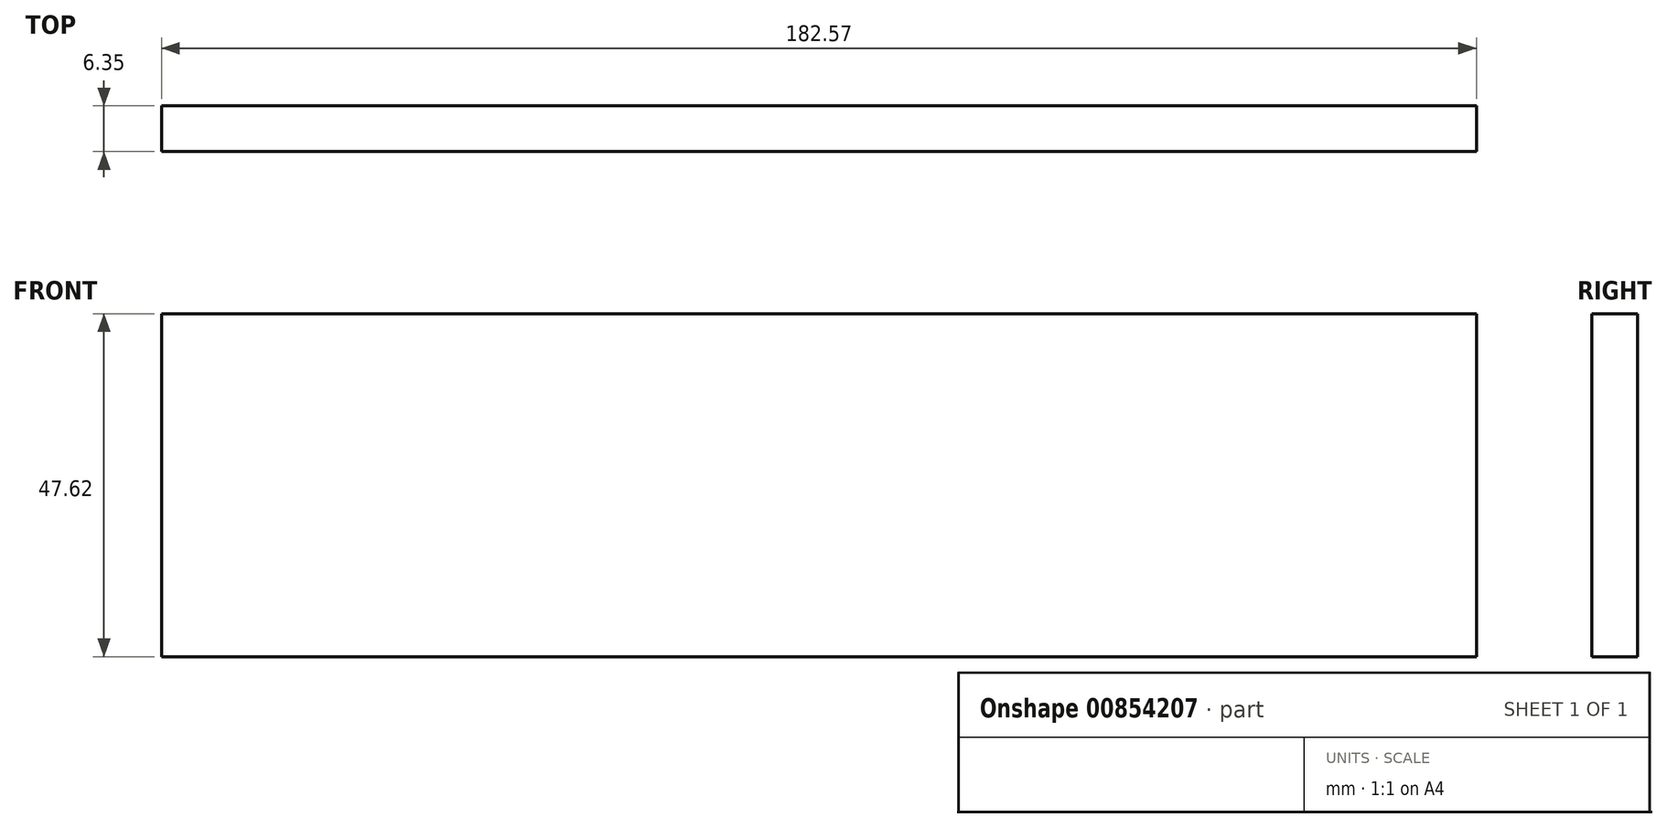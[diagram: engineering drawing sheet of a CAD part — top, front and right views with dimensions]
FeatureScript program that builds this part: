
annotation { "Feature Type Name" : "Feature", "Feature Type Description" : "" }
export const myFeature = defineFeature(function(context is Context, id is Id, definition is map)
    precondition{}
    {
        {
            var Q0;
            Q0=qCreatedBy(makeId("Front.planeOp"),FACE);
            var sketch = newSketch(context, id + "F0", { "sketchPlane" : qUnion([Q0])});
            skLineSegment(sketch, "E0.bottom", {"start": v(-91.29, 23.81) * mm, "end": v(91.28, 23.81) * mm});
            skLineSegment(sketch, "E0.top", {"start": v(-91.29, -23.81) * mm, "end": v(91.28, -23.81) * mm});
            skLineSegment(sketch, "E0.left", {"start": v(-91.29, 23.81) * mm, "end": v(-91.29, -23.81) * mm});
            skLineSegment(sketch, "E0.right", {"start": v(91.28, 23.81) * mm, "end": v(91.28, -23.81) * mm});
            skSolve(sketch);
        }
        {
            var Q0;
            Q0=makeQuery(id+"F0.imprint","IMPRINT",FACE,{"disambiguationData":[TD([[makeQuery(id+"F0.imprint","IMPRINT",EDGE,{"derivedFrom":sQuery(id+"F0.wireOp",EDGE,"E0.bottom")}),-1.0]])]});
            extrude(context, id + "F1", {"entities" : qUnion([Q0]), "depth" : 6.35 * mm, "offsetDistance" : 25.4 * mm});
        }
    });
